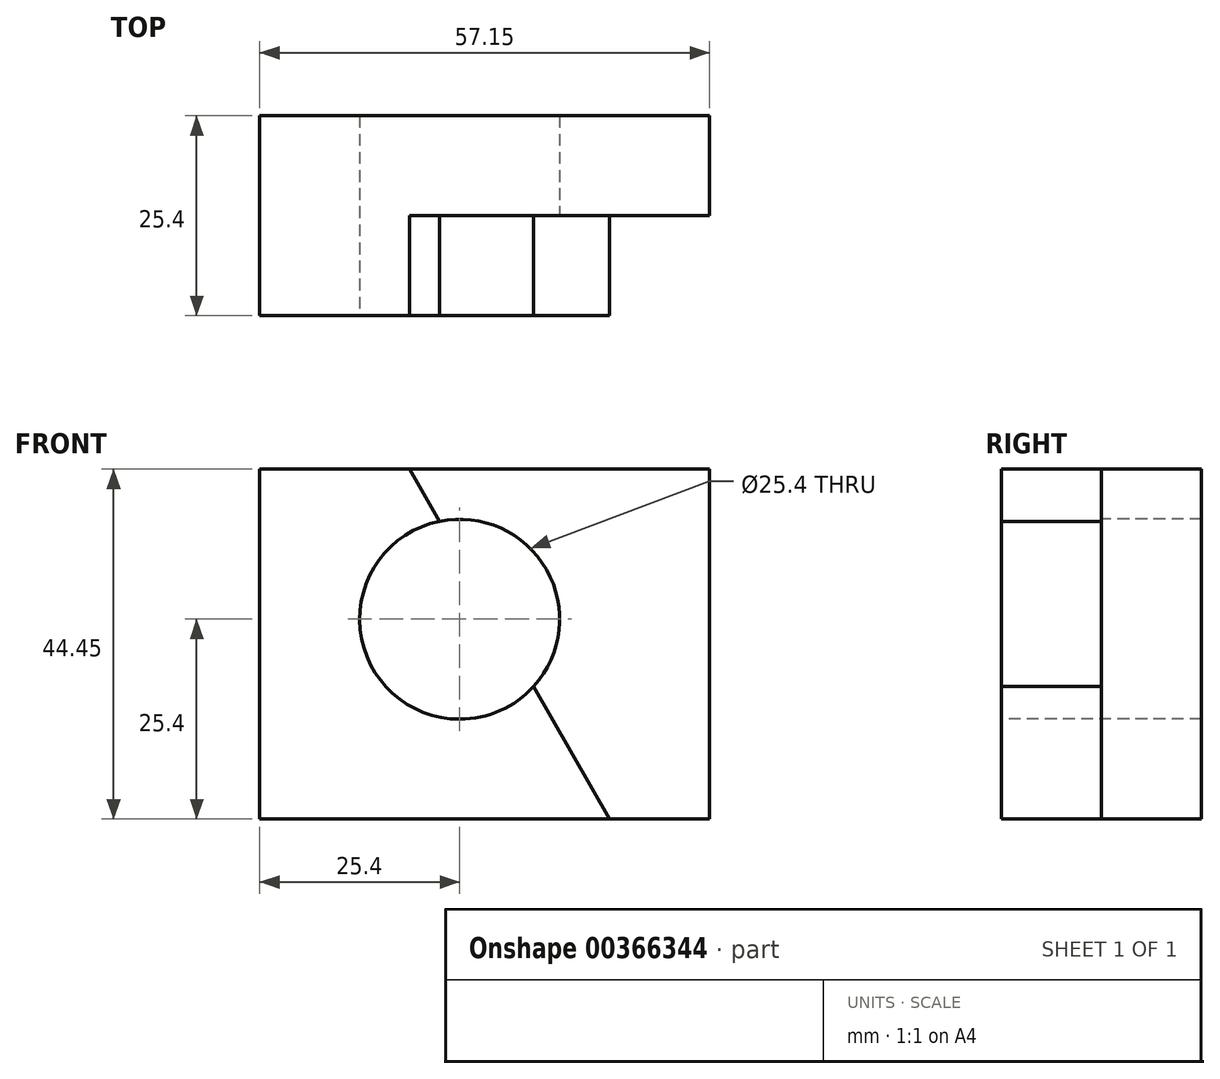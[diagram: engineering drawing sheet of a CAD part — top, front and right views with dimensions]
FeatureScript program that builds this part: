
annotation { "Feature Type Name" : "Feature", "Feature Type Description" : "" }
export const myFeature = defineFeature(function(context is Context, id is Id, definition is map)
    precondition{}
    {
        {
            var Q0;
            Q0=qCreatedBy(makeId("Front.planeOp"),FACE);
            var sketch = newSketch(context, id + "F0", { "sketchPlane" : qUnion([Q0])});
            skLineSegment(sketch, "E0", {"start": v(0, 44.45) * mm, "end": v(0, 0) * mm});
            skLineSegment(sketch, "E1", {"start": v(0, 0) * mm, "end": v(57.15, 0) * mm});
            skLineSegment(sketch, "E2", {"start": v(57.15, 0) * mm, "end": v(57.15, 44.45) * mm});
            skLineSegment(sketch, "E3", {"start": v(57.15, 44.45) * mm, "end": v(0, 44.45) * mm});
            skSolve(sketch);
        }
        {
            var Q0;
            Q0 = qSketchRegion(id + "F0", true);
            extrude(context, id + "F1", {"entities" : qUnion([Q0]), "depth" : 25.4 * mm});
        }
        {
            var Q0;
            Q0=makeQuery(id+"F1.opExtrude","CAP_FACE",FACE,{"disambiguationData":[OSD([sQuery(id+"F0.wireOp",EDGE,"E0"),sQuery(id+"F0.wireOp",EDGE,"E1"),sQuery(id+"F0.wireOp",EDGE,"E2"),sQuery(id+"F0.wireOp",EDGE,"E3")])],"isStart":false});
            var sketch = newSketch(context, id + "F2", { "sketchPlane" : qUnion([Q0])});
            skLineSegment(sketch, "E4", {"start": v(19.05, 44.45) * mm, "end": v(44.45, 0) * mm});
            skSolve(sketch);
        }
        {
            var Q0;
            Q0 = qSketchRegion(id + "F2", true);
            var Q1;
            {var subQ0=sQuery(id+"F2.wireOp",EDGE,"E4");Q1=makeQuery(id+"F2.imprint","IMPRINT",FACE,{"disambiguationData":[TD([[makeQuery(id+"F2.imprint","IMPRINT",EDGE,{"derivedFrom":subQ0}),1.0]])]});}
            extrude(context, id + "F3", {"entities" : qUnion([Q0, Q1]), "operationType" : NewBodyOperationType.REMOVE, "oppositeDirection" : true, "depth" : 12.7 * mm});
        }
        {
            var Q0;
            Q0=makeQuery(id+"F1.opExtrude","CAP_FACE",FACE,{"disambiguationData":[OSD([sQuery(id+"F0.wireOp",EDGE,"E0"),sQuery(id+"F0.wireOp",EDGE,"E1"),sQuery(id+"F0.wireOp",EDGE,"E2"),sQuery(id+"F0.wireOp",EDGE,"E3")])],"isStart":false});
            var sketch = newSketch(context, id + "F4", { "sketchPlane" : qUnion([Q0])});
            skCircle(sketch, "E5", {"center": v(25.4, 25.4) * mm, "radius": 12.7 * mm});
            skSolve(sketch);
        }
        {
            var Q0;
            Q0 = qSketchRegion(id + "F4", true);
            extrude(context, id + "F5", {"entities" : qUnion([Q0]), "operationType" : NewBodyOperationType.REMOVE, "oppositeDirection" : true, "depth" : 25.4 * mm});
        }
    });
